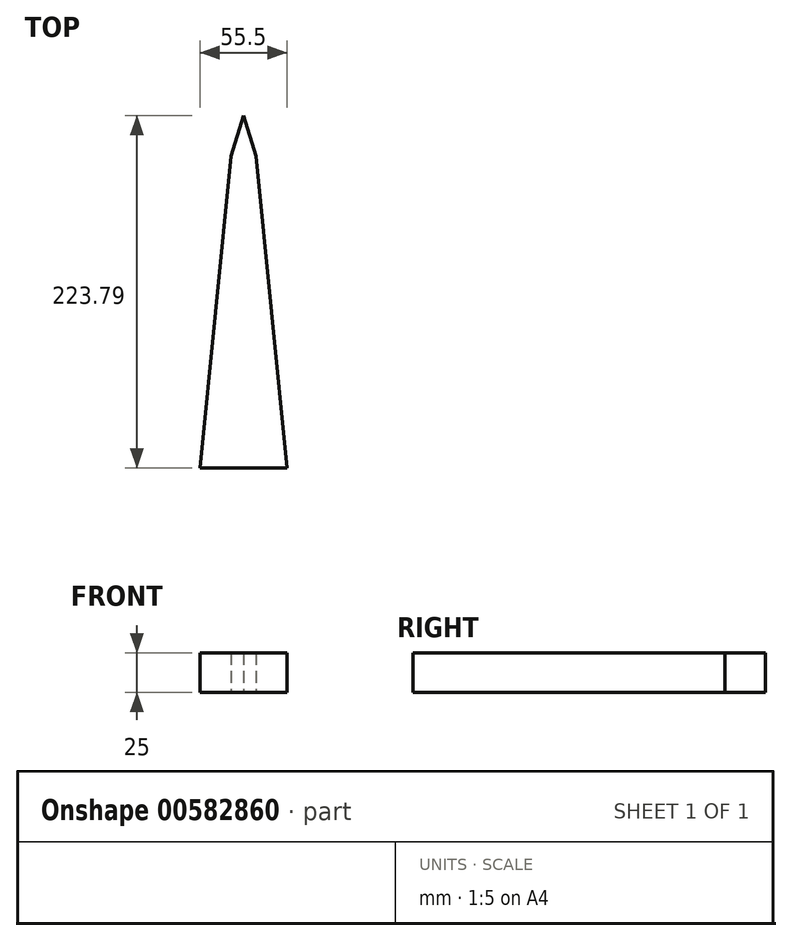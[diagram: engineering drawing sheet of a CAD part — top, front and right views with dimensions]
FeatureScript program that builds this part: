
annotation { "Feature Type Name" : "Feature", "Feature Type Description" : "" }
export const myFeature = defineFeature(function(context is Context, id is Id, definition is map)
    precondition{}
    {
        {
            var Q0;
            Q0=qCreatedBy(makeId("Top.planeOp"),FACE);
            var sketch = newSketch(context, id + "F0", { "sketchPlane" : qUnion([Q0])});
            skLineSegment(sketch, "E0", {"start": v(0, 0) * mm, "end": v(55.5, 0) * mm, "construction": true});
            skLineSegment(sketch, "E1", {"start": v(27.75, 0) * mm, "end": v(27.75, 198) * mm, "construction": true});
            skLineSegment(sketch, "E2", {"start": v(27.75, 198) * mm, "end": v(35.75, 198) * mm});
            skLineSegment(sketch, "E3", {"start": v(35.75, 198) * mm, "end": v(55.5, 0) * mm});
            skLineSegment(sketch, "E4", {"start": v(27.75, 198) * mm, "end": v(19.75, 198) * mm});
            skLineSegment(sketch, "E5", {"start": v(19.75, 198) * mm, "end": v(0, 0) * mm});
            skLineSegment(sketch, "E6", {"start": v(27.75, 198) * mm, "end": v(27.75, 223.79) * mm, "construction": true});
            skLineSegment(sketch, "E7", {"start": v(19.75, 198) * mm, "end": v(27.75, 223.79) * mm});
            skLineSegment(sketch, "E8", {"start": v(27.75, 223.79) * mm, "end": v(35.75, 198) * mm});
            skLineSegment(sketch, "E9", {"start": v(0, 0) * mm, "end": v(55.5, 0) * mm});
            skSolve(sketch);
        }
        {
            var Q0;
            Q0 = qSketchRegion(id + "F0", true);
            extrude(context, id + "F1", {"entities" : qUnion([Q0]), "depth" : 25 * mm, "offsetDistance" : 25 * mm});
        }
        {
            var Q0;
            Q0 = qSketchRegion(id + "F0", true);
            extrude(context, id + "F2", {"entities" : qUnion([Q0]), "operationType" : NewBodyOperationType.ADD, "depth" : 10 * mm, "offsetDistance" : 25 * mm});
        }
    });
